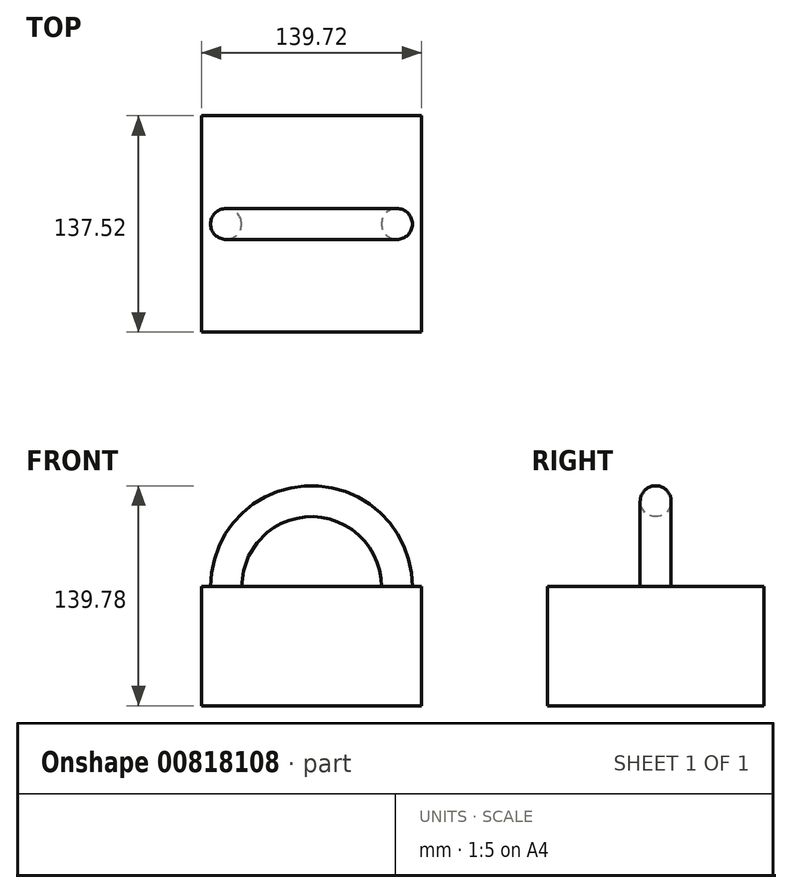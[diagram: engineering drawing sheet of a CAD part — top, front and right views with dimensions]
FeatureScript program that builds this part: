
annotation { "Feature Type Name" : "Feature", "Feature Type Description" : "" }
export const myFeature = defineFeature(function(context is Context, id is Id, definition is map)
    precondition{}
    {
        {
            var Q0;
            Q0=qCreatedBy(makeId("Top.planeOp"),FACE);
            var sketch = newSketch(context, id + "F0", { "sketchPlane" : qUnion([Q0])});
            skLineSegment(sketch, "E0.bottom", {"start": v(69.86, -68.76) * mm, "end": v(-69.86, -68.76) * mm});
            skLineSegment(sketch, "E0.top", {"start": v(69.86, 68.76) * mm, "end": v(-69.86, 68.76) * mm});
            skLineSegment(sketch, "E0.left", {"start": v(69.86, -68.76) * mm, "end": v(69.86, 68.76) * mm});
            skLineSegment(sketch, "E0.right", {"start": v(-69.86, -68.76) * mm, "end": v(-69.86, 68.76) * mm});
            skPoint(sketch, "E0.middle", {"position": v(0, 0) * mm});
            skLineSegment(sketch, "E1", {"start": v(0, 68.76) * mm, "end": v(0, -68.76) * mm});
            skSolve(sketch);
        }
        {
            var Q0;
            Q0=qCreatedBy(makeId("Top.planeOp"),FACE);
            var sketch = newSketch(context, id + "F1", { "sketchPlane" : qUnion([Q0])});
            skCircle(sketch, "E2", {"center": v(54.26, 0) * mm, "radius": 9.82 * mm});
            skSolve(sketch);
        }
        {
            var Q0;
            {var subQ0=sQuery(id+"F0.wireOp",EDGE,"E0.left");Q0=makeQuery(id+"F0.imprint","IMPRINT",FACE,{"disambiguationData":[TD([[makeQuery(id+"F0.imprint","IMPRINT",EDGE,{"derivedFrom":subQ0}),1.0]])]});}
            var Q1;
            {var subQ0=sQuery(id+"F0.wireOp",EDGE,"E0.right");Q1=makeQuery(id+"F0.imprint","IMPRINT",FACE,{"disambiguationData":[TD([[makeQuery(id+"F0.imprint","IMPRINT",EDGE,{"derivedFrom":subQ0}),-1.0]])]});}
            extrude(context, id + "F2", {"entities" : qUnion([Q0, Q1]), "oppositeDirection" : true, "depth" : 75.7 * mm, "offsetDistance" : 25.4 * mm});
        }
        {
            var Q0;
            Q0=qSketchRegion(id+"F1",true);
            var Q1;
            Q1=sQuery(id+"F0.wireOp",EDGE,"E1");
            revolve(context, id + "F3", {"operationType" : NewBodyOperationType.ADD, "surfaceOperationType" : NewSurfaceOperationType.NEW, "entities" : qUnion([Q0]), "axis" : qUnion([Q1]), "revolveType" : RevolveType.FULL});
        }
    });
